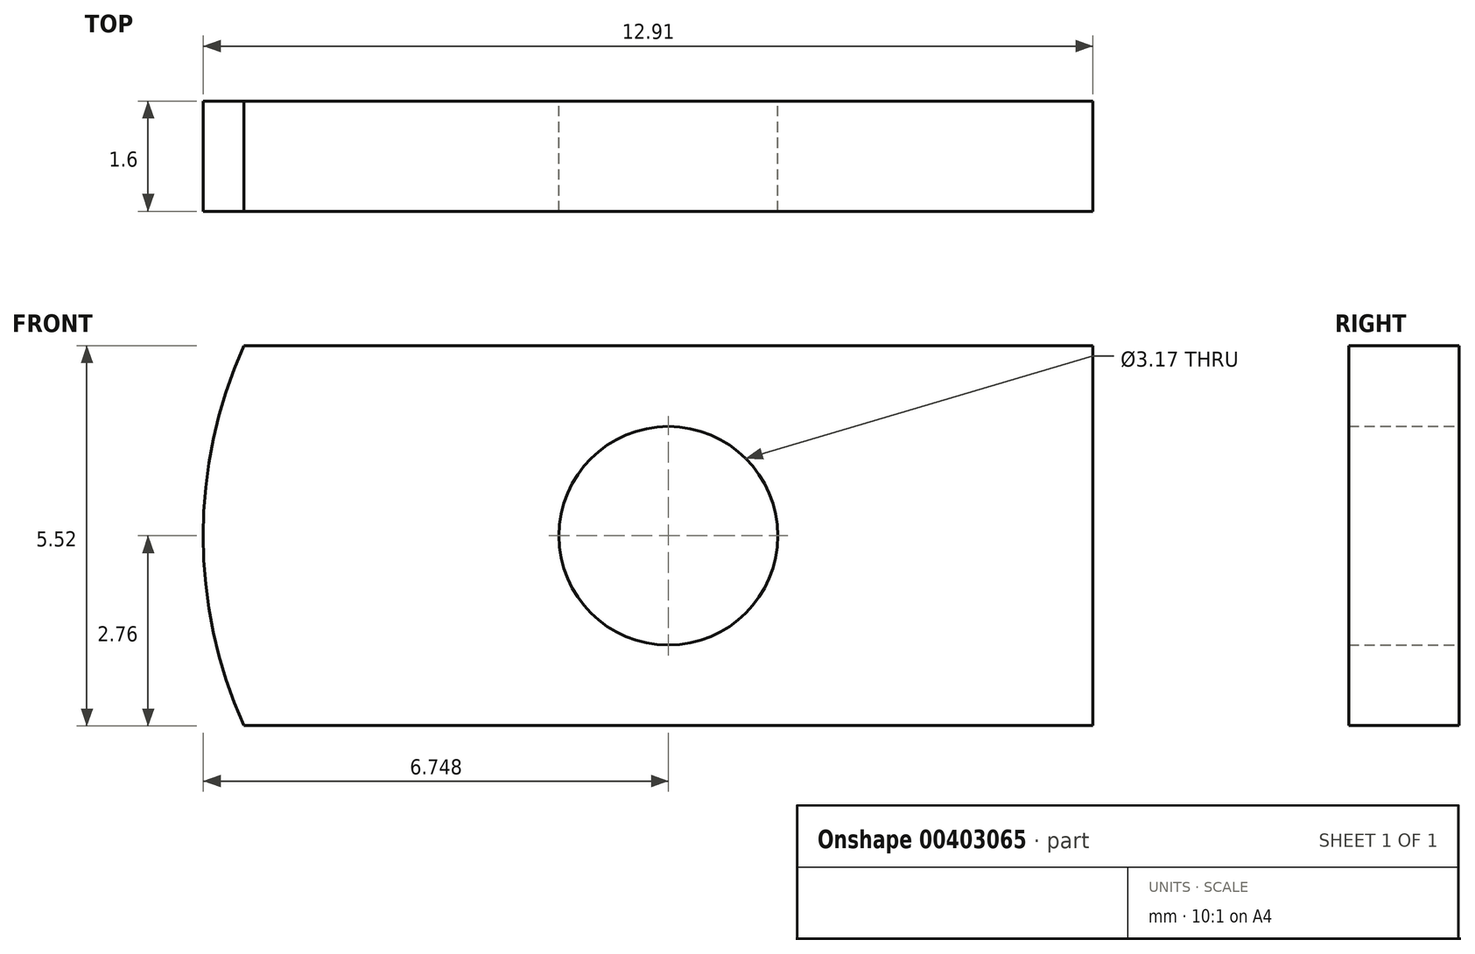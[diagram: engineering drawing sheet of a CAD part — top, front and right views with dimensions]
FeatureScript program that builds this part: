
annotation { "Feature Type Name" : "Feature", "Feature Type Description" : "" }
export const myFeature = defineFeature(function(context is Context, id is Id, definition is map)
    precondition{}
    {
        {
            var Q0;
            Q0=qCreatedBy(makeId("Front.planeOp"),FACE);
            var sketch = newSketch(context, id + "F0", { "sketchPlane" : qUnion([Q0])});
            skArc(sketch, "E0", {"start": v(-6.08, 2.76) * mm, "mid": v(-6.67, 0) * mm, "end": v(-6.08, -2.76) * mm});
            skCircle(sketch, "E1", {"center": v(0.08, 0) * mm, "radius": 1.59 * mm});
            skLineSegment(sketch, "E2", {"start": v(-6.08, 2.76) * mm, "end": v(6.24, 2.76) * mm});
            skLineSegment(sketch, "E3", {"start": v(6.24, 2.76) * mm, "end": v(6.24, -2.76) * mm});
            skLineSegment(sketch, "E4", {"start": v(6.24, -2.76) * mm, "end": v(-6.08, -2.76) * mm});
            skSolve(sketch);
        }
        {
            var Q0;
            Q0=makeQuery(id+"F0.imprint","IMPRINT",FACE,{"disambiguationData":[TD([[makeQuery(id+"F0.imprint","IMPRINT",EDGE,{"derivedFrom":sQuery(id+"F0.wireOp",EDGE,"E0")}),1.0]])]});
            extrude(context, id + "F1", {"entities" : qUnion([Q0]), "endBound" : BoundingType.SYMMETRIC, "depth" : 1.6 * mm});
        }
    });
